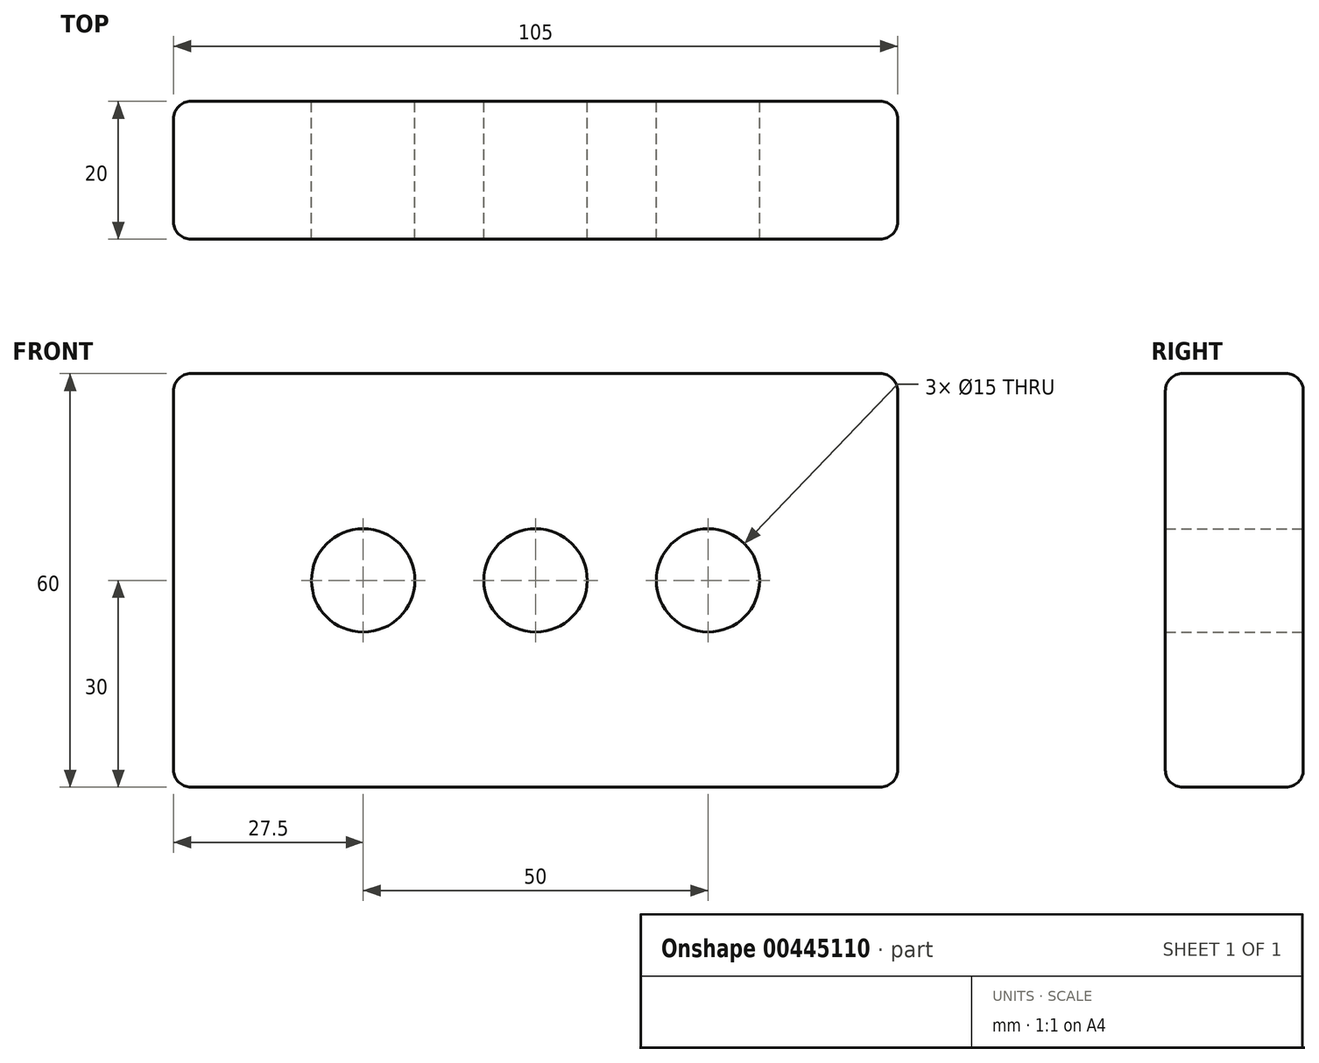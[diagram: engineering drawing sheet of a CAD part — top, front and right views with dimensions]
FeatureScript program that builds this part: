
annotation { "Feature Type Name" : "Feature", "Feature Type Description" : "" }
export const myFeature = defineFeature(function(context is Context, id is Id, definition is map)
    precondition{}
    {
        {
            var Q0;
            Q0=qCreatedBy(makeId("Front.planeOp"),FACE);
            var sketch = newSketch(context, id + "F0", { "sketchPlane" : qUnion([Q0])});
            skLineSegment(sketch, "E0.bottom", {"start": v(0, 0) * mm, "end": v(52.5, 0) * mm});
            skLineSegment(sketch, "E0.top", {"start": v(0, 60) * mm, "end": v(52.5, 60) * mm});
            skLineSegment(sketch, "E0.left", {"start": v(0, 0) * mm, "end": v(0, 60) * mm});
            skLineSegment(sketch, "E0.right", {"start": v(52.5, 0) * mm, "end": v(52.5, 60) * mm});
            skLineSegment(sketch, "E1.bottom", {"start": v(0, 0) * mm, "end": v(-52.5, 0) * mm});
            skLineSegment(sketch, "E1.top", {"start": v(0, 60) * mm, "end": v(-52.5, 60) * mm});
            skLineSegment(sketch, "E1.right", {"start": v(-52.5, 0) * mm, "end": v(-52.5, 60) * mm});
            skSolve(sketch);
        }
        {
            var Q0;
            Q0 = qSketchRegion(id + "F0", true);
            extrude(context, id + "F1", {"entities" : qUnion([Q0]), "depth" : 20 * mm});
        }
        {
            var Q0;
            Q0=qCreatedBy(makeId("Front.planeOp"),FACE);
            var sketch = newSketch(context, id + "F2", { "sketchPlane" : qUnion([Q0])});
            skLineSegment(sketch, "E2", {"start": v(0, 60) * mm, "end": v(0, 0) * mm});
            skLineSegment(sketch, "E3", {"start": v(0, 0) * mm, "end": v(0, 30) * mm});
            skCircle(sketch, "E4", {"center": v(0, 30) * mm, "radius": 7.5 * mm});
            skLineSegment(sketch, "E5", {"start": v(52.56, 30) * mm, "end": v(-52.44, 30) * mm});
            skLineSegment(sketch, "E6", {"start": v(7.5, 30) * mm, "end": v(17.5, 30) * mm});
            skLineSegment(sketch, "E7", {"start": v(17.5, 30) * mm, "end": v(25, 30) * mm});
            skCircle(sketch, "E8", {"center": v(25, 30) * mm, "radius": 7.5 * mm});
            skLineSegment(sketch, "E9", {"start": v(-7.5, 30) * mm, "end": v(-25, 30) * mm});
            skCircle(sketch, "E10", {"center": v(-25, 30) * mm, "radius": 7.5 * mm});
            skSolve(sketch);
        }
        {
            var Q0;
            Q0 = qSketchRegion(id + "F2", true);
            extrude(context, id + "F3", {"entities" : qUnion([Q0]), "operationType" : NewBodyOperationType.REMOVE, "depth" : 25 * mm});
        }
        {
            var Q0;
            Q0=makeQuery(id+"F1.opExtrude","SWEPT_EDGE",EDGE,{"disambiguationData":[OSD([sQuery(id+"F0.wireOp",EDGE,"E0.top"),sQuery(id+"F0.wireOp",EDGE,"E0.right")])]});
            var Q1;
            Q1=makeQuery(id+"F1.opExtrude","SWEPT_FACE",FACE,{"disambiguationData":[OSD([sQuery(id+"F0.wireOp",EDGE,"E0.top"),sQuery(id+"F0.wireOp",EDGE,"E1.top")])]});
            var Q2;
            Q2=makeQuery(id+"F1.opExtrude","SWEPT_FACE",FACE,{"disambiguationData":[OSD([sQuery(id+"F0.wireOp",EDGE,"E0.right")])]});
            var Q3;
            Q3=makeQuery(id+"F1.opExtrude","SWEPT_FACE",FACE,{"disambiguationData":[OSD([sQuery(id+"F0.wireOp",EDGE,"E0.bottom"),sQuery(id+"F0.wireOp",EDGE,"E1.bottom")])]});
            var Q4;
            Q4=makeQuery(id+"F1.opExtrude","SWEPT_FACE",FACE,{"disambiguationData":[OSD([sQuery(id+"F0.wireOp",EDGE,"E1.right")])]});
            fillet(context, id + "F4", {"entities" : qUnion([Q0, Q1, Q2, Q3, Q4]), "radius" : 2.5 * mm, "tangentPropagation" : true, "allowEdgeOverflow" : false});
        }
    });
